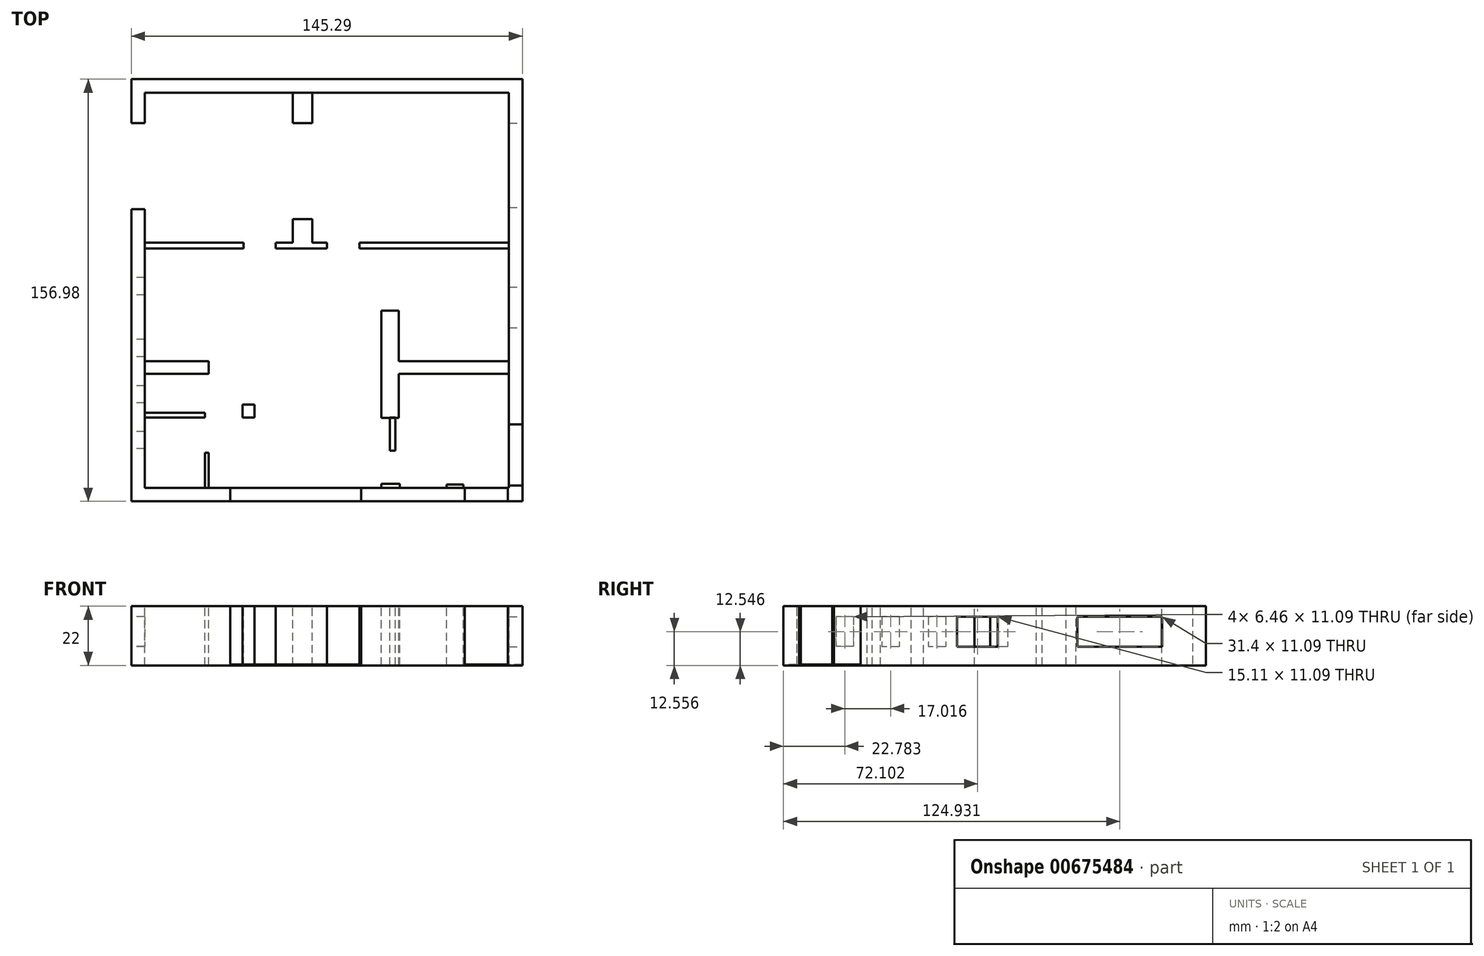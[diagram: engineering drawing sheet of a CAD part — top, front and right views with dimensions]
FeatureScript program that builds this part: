
annotation { "Feature Type Name" : "Feature", "Feature Type Description" : "" }
export const myFeature = defineFeature(function(context is Context, id is Id, definition is map)
    precondition{}
    {
        {
            var Q0;
            Q0=qCreatedBy(makeId("Top.planeOp"),FACE);
            var sketch = newSketch(context, id + "F0", { "sketchPlane" : qUnion([Q0])});
            skLineSegment(sketch, "E0.bottom", {"start": v(-72.65, -85.85) * mm, "end": v(72.64, -85.85) * mm});
            skLineSegment(sketch, "E0.top", {"start": v(-72.65, 71.13) * mm, "end": v(72.64, 71.13) * mm});
            skLineSegment(sketch, "E0.left", {"start": v(-72.65, -85.85) * mm, "end": v(-72.65, 71.13) * mm});
            skLineSegment(sketch, "E0.right", {"start": v(72.64, -85.85) * mm, "end": v(72.64, 71.13) * mm});
            skLineSegment(sketch, "E1.0", {"start": v(-67.65, 66.13) * mm, "end": v(67.64, 66.13) * mm});
            skLineSegment(sketch, "E1.1", {"start": v(-67.65, -80.85) * mm, "end": v(-67.65, 66.13) * mm});
            skLineSegment(sketch, "E1.2", {"start": v(-67.65, -80.85) * mm, "end": v(67.64, -80.85) * mm});
            skLineSegment(sketch, "E1.3", {"start": v(67.64, -80.85) * mm, "end": v(67.64, 66.13) * mm});
            skSolve(sketch);
        }
        {
            var Q0;
            Q0=makeQuery(id+"F0.imprint","IMPRINT",FACE,{"disambiguationData":[TD([[makeQuery(id+"F0.imprint","IMPRINT",EDGE,{"derivedFrom":sQuery(id+"F0.wireOp",EDGE,"E0.bottom")}),1.0]])]});
            extrude(context, id + "F1", {"entities" : qUnion([Q0]), "depth" : 22 * mm, "offsetDistance" : 25 * mm});
        }
        {
            var Q0;
            Q0=makeQuery(id+"F1.opExtrude","CAP_FACE",FACE,{"disambiguationData":[OSD([sQuery(id+"F0.wireOp",EDGE,"E0.bottom"),sQuery(id+"F0.wireOp",EDGE,"E0.top"),sQuery(id+"F0.wireOp",EDGE,"E0.left"),sQuery(id+"F0.wireOp",EDGE,"E0.right"),sQuery(id+"F0.wireOp",EDGE,"E1.0"),sQuery(id+"F0.wireOp",EDGE,"E1.1"),sQuery(id+"F0.wireOp",EDGE,"E1.2"),sQuery(id+"F0.wireOp",EDGE,"E1.3")])],"isStart":false});
            var sketch = newSketch(context, id + "F2", { "sketchPlane" : qUnion([Q0])});
            skLineSegment(sketch, "E2.bottom", {"start": v(-67.65, -33.8) * mm, "end": v(67.64, -33.8) * mm});
            skLineSegment(sketch, "E2.top", {"start": v(-67.65, -38.4) * mm, "end": v(67.64, -38.4) * mm});
            skLineSegment(sketch, "E2.left", {"start": v(-67.65, -33.8) * mm, "end": v(-67.65, -38.4) * mm});
            skLineSegment(sketch, "E2.right", {"start": v(67.64, -33.8) * mm, "end": v(67.64, -38.4) * mm});
            skLineSegment(sketch, "E3.bottom", {"start": v(20.19, -54.82) * mm, "end": v(26.7, -54.82) * mm});
            skLineSegment(sketch, "E3.top", {"start": v(20.19, -14.94) * mm, "end": v(26.7, -14.94) * mm});
            skLineSegment(sketch, "E3.left", {"start": v(20.19, -54.82) * mm, "end": v(20.19, -14.94) * mm});
            skLineSegment(sketch, "E3.right", {"start": v(26.7, -54.82) * mm, "end": v(26.7, -14.94) * mm});
            skLineSegment(sketch, "E4.bottom", {"start": v(-12.7, 66.13) * mm, "end": v(-5.43, 66.13) * mm});
            skLineSegment(sketch, "E4.top", {"start": v(-12.7, 54.76) * mm, "end": v(-5.43, 54.76) * mm});
            skLineSegment(sketch, "E4.left", {"start": v(-12.7, 66.13) * mm, "end": v(-12.7, 54.76) * mm});
            skLineSegment(sketch, "E4.right", {"start": v(-5.43, 66.13) * mm, "end": v(-5.43, 54.76) * mm});
            skLineSegment(sketch, "E5.bottom", {"start": v(-12.7, 19.1) * mm, "end": v(-5.43, 19.1) * mm});
            skLineSegment(sketch, "E5.top", {"start": v(-12.7, 8.13) * mm, "end": v(-5.43, 8.13) * mm});
            skLineSegment(sketch, "E5.left", {"start": v(-12.7, 19.1) * mm, "end": v(-12.7, 8.13) * mm});
            skLineSegment(sketch, "E5.right", {"start": v(-5.43, 19.1) * mm, "end": v(-5.43, 8.13) * mm});
            skLineSegment(sketch, "E6", {"start": v(-43.96, -38.4) * mm, "end": v(-43.96, -33.8) * mm});
            skLineSegment(sketch, "E7.bottom", {"start": v(-67.65, 10.3) * mm, "end": v(67.64, 10.3) * mm});
            skLineSegment(sketch, "E7.top", {"start": v(-67.65, 8.13) * mm, "end": v(67.64, 8.13) * mm});
            skLineSegment(sketch, "E7.left", {"start": v(-67.65, 10.3) * mm, "end": v(-67.65, 8.13) * mm});
            skLineSegment(sketch, "E7.right", {"start": v(67.64, 10.3) * mm, "end": v(67.64, 8.13) * mm});
            skLineSegment(sketch, "E8.bottom", {"start": v(19.78, 8.13) * mm, "end": v(26.7, 8.13) * mm});
            skLineSegment(sketch, "E8.top", {"start": v(19.78, -2.58) * mm, "end": v(26.7, -2.58) * mm});
            skLineSegment(sketch, "E8.left", {"start": v(19.78, 8.13) * mm, "end": v(19.78, -2.58) * mm});
            skLineSegment(sketch, "E8.right", {"start": v(26.7, 8.13) * mm, "end": v(26.7, -2.58) * mm});
            skLineSegment(sketch, "E9.bottom", {"start": v(-43.96, -38.4) * mm, "end": v(-45.35, -38.4) * mm});
            skLineSegment(sketch, "E9.top", {"start": v(-43.96, -80.85) * mm, "end": v(-45.35, -80.85) * mm});
            skLineSegment(sketch, "E9.left", {"start": v(-43.96, -38.4) * mm, "end": v(-43.96, -80.85) * mm});
            skLineSegment(sketch, "E9.right", {"start": v(-45.35, -38.4) * mm, "end": v(-45.35, -80.85) * mm});
            skLineSegment(sketch, "E10.bottom", {"start": v(-67.65, -52.88) * mm, "end": v(-45.35, -52.88) * mm});
            skLineSegment(sketch, "E10.top", {"start": v(-67.65, -54.74) * mm, "end": v(-45.35, -54.74) * mm});
            skLineSegment(sketch, "E10.left", {"start": v(-67.65, -52.88) * mm, "end": v(-67.65, -54.74) * mm});
            skLineSegment(sketch, "E10.right", {"start": v(-45.35, -52.88) * mm, "end": v(-45.35, -54.74) * mm});
            skLineSegment(sketch, "E11.bottom", {"start": v(-45.35, -52.88) * mm, "end": v(-48.5, -52.88) * mm});
            skLineSegment(sketch, "E11.top", {"start": v(-45.35, -49.82) * mm, "end": v(-48.5, -49.82) * mm});
            skLineSegment(sketch, "E11.left", {"start": v(-45.35, -52.88) * mm, "end": v(-45.35, -49.82) * mm});
            skLineSegment(sketch, "E11.right", {"start": v(-48.5, -52.88) * mm, "end": v(-48.5, -49.82) * mm});
            skLineSegment(sketch, "E12.bottom", {"start": v(-31.4, -49.82) * mm, "end": v(-26.87, -49.82) * mm});
            skLineSegment(sketch, "E12.top", {"start": v(-31.4, -54.74) * mm, "end": v(-26.87, -54.74) * mm});
            skLineSegment(sketch, "E12.left", {"start": v(-31.4, -49.82) * mm, "end": v(-31.4, -54.74) * mm});
            skLineSegment(sketch, "E12.right", {"start": v(-26.87, -49.82) * mm, "end": v(-26.87, -54.74) * mm});
            skLineSegment(sketch, "E13.bottom", {"start": v(3.94, -49.82) * mm, "end": v(8.38, -49.82) * mm});
            skLineSegment(sketch, "E13.top", {"start": v(3.94, -54.74) * mm, "end": v(8.38, -54.74) * mm});
            skLineSegment(sketch, "E13.left", {"start": v(3.94, -49.82) * mm, "end": v(3.94, -54.74) * mm});
            skLineSegment(sketch, "E13.right", {"start": v(8.38, -49.82) * mm, "end": v(8.38, -54.74) * mm});
            skPoint(sketch, "E14.firstSnap0", {"position": v(23.45, -54.82) * mm});
            skLineSegment(sketch, "E14.bottom", {"start": v(23.45, -54.74) * mm, "end": v(25.37, -54.74) * mm});
            skLineSegment(sketch, "E14.top", {"start": v(23.45, -67.02) * mm, "end": v(25.37, -67.02) * mm});
            skLineSegment(sketch, "E14.left", {"start": v(23.45, -54.74) * mm, "end": v(23.45, -67.02) * mm});
            skLineSegment(sketch, "E14.right", {"start": v(25.37, -54.74) * mm, "end": v(25.37, -67.02) * mm});
            skLineSegment(sketch, "E15.bottom", {"start": v(47.7, -38.4) * mm, "end": v(49.52, -38.4) * mm});
            skLineSegment(sketch, "E15.top", {"start": v(47.7, -65.4) * mm, "end": v(49.52, -65.4) * mm});
            skLineSegment(sketch, "E15.left", {"start": v(47.7, -38.4) * mm, "end": v(47.7, -65.4) * mm});
            skLineSegment(sketch, "E15.right", {"start": v(49.52, -38.4) * mm, "end": v(49.52, -65.4) * mm});
            skLineSegment(sketch, "E16.bottom", {"start": v(-46.06, -33.8) * mm, "end": v(-43.96, -33.8) * mm});
            skLineSegment(sketch, "E16.top", {"start": v(-46.06, -17.64) * mm, "end": v(-43.96, -17.64) * mm});
            skLineSegment(sketch, "E16.left", {"start": v(-46.06, -33.8) * mm, "end": v(-46.06, -17.64) * mm});
            skLineSegment(sketch, "E16.right", {"start": v(-43.96, -33.8) * mm, "end": v(-43.96, -17.64) * mm});
            skLineSegment(sketch, "E17.bottom", {"start": v(-30.98, 10.3) * mm, "end": v(-19.04, 10.3) * mm});
            skLineSegment(sketch, "E17.top", {"start": v(-30.98, 8.13) * mm, "end": v(-19.04, 8.13) * mm});
            skLineSegment(sketch, "E17.left", {"start": v(-30.98, 10.3) * mm, "end": v(-30.98, 8.13) * mm});
            skLineSegment(sketch, "E17.right", {"start": v(-19.04, 10.3) * mm, "end": v(-19.04, 8.13) * mm});
            skLineSegment(sketch, "E18.bottom", {"start": v(0, 10.3) * mm, "end": v(12.04, 10.3) * mm});
            skLineSegment(sketch, "E18.top", {"start": v(0, 8.13) * mm, "end": v(12.04, 8.13) * mm});
            skLineSegment(sketch, "E18.left", {"start": v(0, 10.3) * mm, "end": v(0, 8.13) * mm});
            skLineSegment(sketch, "E18.right", {"start": v(12.04, 10.3) * mm, "end": v(12.04, 8.13) * mm});
            skLineSegment(sketch, "E19.bottom", {"start": v(-45.35, -39.31) * mm, "end": v(-43.96, -39.31) * mm});
            skLineSegment(sketch, "E19.top", {"start": v(-45.35, -48.84) * mm, "end": v(-43.96, -48.84) * mm});
            skLineSegment(sketch, "E19.left", {"start": v(-45.35, -39.31) * mm, "end": v(-45.35, -48.84) * mm});
            skLineSegment(sketch, "E19.right", {"start": v(-43.96, -39.31) * mm, "end": v(-43.96, -48.84) * mm});
            skLineSegment(sketch, "E20.bottom", {"start": v(-45.35, -56.47) * mm, "end": v(-43.56, -56.47) * mm});
            skLineSegment(sketch, "E20.top", {"start": v(-45.35, -67.73) * mm, "end": v(-43.56, -67.73) * mm});
            skLineSegment(sketch, "E20.left", {"start": v(-45.35, -56.47) * mm, "end": v(-45.35, -67.73) * mm});
            skLineSegment(sketch, "E20.right", {"start": v(-43.56, -56.47) * mm, "end": v(-43.56, -67.73) * mm});
            skLineSegment(sketch, "E21.bottom", {"start": v(20.19, -80.85) * mm, "end": v(27.13, -80.85) * mm});
            skLineSegment(sketch, "E21.top", {"start": v(20.19, -79.38) * mm, "end": v(27.13, -79.38) * mm});
            skLineSegment(sketch, "E21.left", {"start": v(20.19, -80.85) * mm, "end": v(20.19, -79.38) * mm});
            skLineSegment(sketch, "E21.right", {"start": v(27.13, -80.85) * mm, "end": v(27.13, -79.38) * mm});
            skLineSegment(sketch, "E22.bottom", {"start": v(44.44, -80.85) * mm, "end": v(50.77, -80.85) * mm});
            skLineSegment(sketch, "E22.top", {"start": v(44.44, -79.58) * mm, "end": v(50.77, -79.58) * mm});
            skLineSegment(sketch, "E22.left", {"start": v(44.44, -80.85) * mm, "end": v(44.44, -79.58) * mm});
            skLineSegment(sketch, "E22.right", {"start": v(50.77, -80.85) * mm, "end": v(50.77, -79.58) * mm});
            skLineSegment(sketch, "E23.bottom", {"start": v(23.66, -79.38) * mm, "end": v(25.37, -79.38) * mm});
            skLineSegment(sketch, "E23.top", {"start": v(23.66, -77.51) * mm, "end": v(25.37, -77.51) * mm});
            skLineSegment(sketch, "E23.left", {"start": v(23.66, -79.38) * mm, "end": v(23.66, -77.51) * mm});
            skLineSegment(sketch, "E23.right", {"start": v(25.37, -79.38) * mm, "end": v(25.37, -77.51) * mm});
            skLineSegment(sketch, "E24.bottom", {"start": v(47.7, -79.58) * mm, "end": v(49.52, -79.58) * mm});
            skLineSegment(sketch, "E24.top", {"start": v(47.7, -77.8) * mm, "end": v(49.52, -77.8) * mm});
            skLineSegment(sketch, "E24.left", {"start": v(47.7, -79.58) * mm, "end": v(47.7, -77.8) * mm});
            skLineSegment(sketch, "E24.right", {"start": v(49.52, -79.58) * mm, "end": v(49.52, -77.8) * mm});
            skSolve(sketch);
        }
        {
            var Q0;
            {var subQ0=sQuery(id+"F2.wireOp",EDGE,"E2.left");Q0=makeQuery(id+"F2.imprint","IMPRINT",FACE,{"disambiguationData":[TD([[makeQuery(id+"F2.imprint","IMPRINT",EDGE,{"derivedFrom":subQ0}),-1.0]])]});}
            var Q1;
            Q1=makeQuery(id+"F2.imprint","IMPRINT",FACE,{"disambiguationData":[TD([[makeQuery(id+"F2.imprint","IMPRINT",EDGE,{"derivedFrom":sQuery(id+"F2.wireOp",EDGE,"E5.bottom")}),-1.0]])]});
            var Q2;
            Q2=makeQuery(id+"F2.imprint","IMPRINT",FACE,{"disambiguationData":[TD([[makeQuery(id+"F2.imprint","IMPRINT",EDGE,{"derivedFrom":sQuery(id+"F2.wireOp",EDGE,"E4.bottom")}),-1.0]])]});
            var Q3;
            {var subQ5=sQuery(id+"F2.wireOp",EDGE,"E3.top");Q3=makeQuery(id+"F2.imprint","IMPRINT",FACE,{"disambiguationData":[TD([[makeQuery(id+"F2.imprint","IMPRINT",EDGE,{"derivedFrom":subQ5}),-1.0]])]});}
            var Q4;
            {var subQ0=sQuery(id+"F2.wireOp",EDGE,"E3.left");var subQ1=sQuery(id+"F2.wireOp",EDGE,"E2.bottom");var subQ2=makeQuery(id+"F2.imprint","INTERSECT",VERTEX,{"derivedFrom":[subQ1,subQ0]});Q4=makeQuery(id+"F2.imprint","IMPRINT",FACE,{"disambiguationData":[TD([[makeQuery(id+"F2.imprint","IMPRINT",EDGE,{"disambiguationData":[TD([[subQ2,-1.0]])],"derivedFrom":subQ1}),-1.0]])]});}
            var Q5;
            {var subQ5=sQuery(id+"F2.wireOp",EDGE,"E3.bottom");Q5=makeQuery(id+"F2.imprint","IMPRINT",FACE,{"disambiguationData":[TD([[makeQuery(id+"F2.imprint","IMPRINT",EDGE,{"derivedFrom":subQ5}),1.0]])]});}
            var Q6;
            {var subQ0=sQuery(id+"F2.wireOp",EDGE,"E2.right");Q6=makeQuery(id+"F2.imprint","IMPRINT",FACE,{"disambiguationData":[TD([[makeQuery(id+"F2.imprint","IMPRINT",EDGE,{"derivedFrom":subQ0}),1.0]])]});}
            var Q7;
            Q7=makeQuery(id+"F2.imprint","IMPRINT",FACE,{"disambiguationData":[TD([[makeQuery(id+"F2.imprint","IMPRINT",EDGE,{"derivedFrom":sQuery(id+"F2.wireOp",EDGE,"E11.bottom")}),-1.0]])]});
            var Q8;
            {var subQ3=sQuery(id+"F2.wireOp",EDGE,"E10.right");Q8=makeQuery(id+"F2.imprint","IMPRINT",FACE,{"disambiguationData":[TD([[makeQuery(id+"F2.imprint","IMPRINT",EDGE,{"derivedFrom":subQ3}),1.0]])]});}
            var Q9;
            Q9=makeQuery(id+"F2.imprint","IMPRINT",FACE,{"disambiguationData":[TD([[makeQuery(id+"F2.imprint","IMPRINT",EDGE,{"derivedFrom":sQuery(id+"F2.wireOp",EDGE,"E10.bottom")}),-1.0]])]});
            var Q10;
            {var subQ0=sQuery(id+"F2.wireOp",EDGE,"E9.top");Q10=makeQuery(id+"F2.imprint","IMPRINT",FACE,{"disambiguationData":[TD([[makeQuery(id+"F2.imprint","IMPRINT",EDGE,{"derivedFrom":subQ0}),1.0]])]});}
            var Q11;
            Q11=makeQuery(id+"F2.imprint","IMPRINT",FACE,{"disambiguationData":[TD([[makeQuery(id+"F2.imprint","IMPRINT",EDGE,{"derivedFrom":sQuery(id+"F2.wireOp",EDGE,"E12.bottom")}),-1.0]])]});
            var Q12;
            {var subQ0=sQuery(id+"F2.wireOp",EDGE,"E7.left");Q12=makeQuery(id+"F2.imprint","IMPRINT",FACE,{"disambiguationData":[TD([[makeQuery(id+"F2.imprint","IMPRINT",EDGE,{"derivedFrom":subQ0}),-1.0]])]});}
            var Q13;
            {var subQ5=sQuery(id+"F2.wireOp",EDGE,"E17.right");Q13=makeQuery(id+"F2.imprint","IMPRINT",FACE,{"disambiguationData":[TD([[makeQuery(id+"F2.imprint","IMPRINT",EDGE,{"derivedFrom":subQ5}),1.0]])]});}
            var Q14;
            {var subQ0=sQuery(id+"F2.wireOp",EDGE,"E7.top");var subQ1=sQuery(id+"F2.wireOp",EDGE,"E5.left");var subQ2=makeQuery(id+"F2.imprint","INTERSECT",VERTEX,{"derivedFrom":[subQ1,subQ0]});Q14=makeQuery(id+"F2.imprint","IMPRINT",FACE,{"disambiguationData":[TD([[makeQuery(id+"F2.imprint","IMPRINT",EDGE,{"disambiguationData":[TD([[subQ2,1.0]])],"derivedFrom":subQ1}),1.0]])]});}
            var Q15;
            {var subQ5=sQuery(id+"F2.wireOp",EDGE,"E18.left");Q15=makeQuery(id+"F2.imprint","IMPRINT",FACE,{"disambiguationData":[TD([[makeQuery(id+"F2.imprint","IMPRINT",EDGE,{"derivedFrom":subQ5}),-1.0]])]});}
            var Q16;
            {var subQ0=sQuery(id+"F2.wireOp",EDGE,"E7.right");Q16=makeQuery(id+"F2.imprint","IMPRINT",FACE,{"disambiguationData":[TD([[makeQuery(id+"F2.imprint","IMPRINT",EDGE,{"derivedFrom":subQ0}),1.0]])]});}
            var Q17;
            Q17=makeQuery(id+"F2.imprint","IMPRINT",FACE,{"disambiguationData":[TD([[makeQuery(id+"F2.imprint","IMPRINT",EDGE,{"derivedFrom":sQuery(id+"F2.wireOp",EDGE,"E8.bottom")}),-1.0]])]});
            var Q18;
            Q18=makeQuery(id+"F2.imprint","IMPRINT",FACE,{"disambiguationData":[TD([[makeQuery(id+"F2.imprint","IMPRINT",EDGE,{"derivedFrom":sQuery(id+"F2.wireOp",EDGE,"E21.bottom")}),1.0]])]});
            var Q19;
            Q19=makeQuery(id+"F2.imprint","IMPRINT",FACE,{"disambiguationData":[TD([[makeQuery(id+"F2.imprint","IMPRINT",EDGE,{"derivedFrom":sQuery(id+"F2.wireOp",EDGE,"E23.bottom")}),1.0]])]});
            var Q20;
            {var subQ5=sQuery(id+"F2.wireOp",EDGE,"E14.top");Q20=makeQuery(id+"F2.imprint","IMPRINT",FACE,{"disambiguationData":[TD([[makeQuery(id+"F2.imprint","IMPRINT",EDGE,{"derivedFrom":subQ5}),1.0]])]});}
            var Q21;
            Q21=makeQuery(id+"F2.imprint","IMPRINT",FACE,{"disambiguationData":[TD([[makeQuery(id+"F2.imprint","IMPRINT",EDGE,{"derivedFrom":sQuery(id+"F2.wireOp",EDGE,"E15.bottom")}),-1.0]])]});
            var Q22;
            Q22=makeQuery(id+"F2.imprint","IMPRINT",FACE,{"disambiguationData":[TD([[makeQuery(id+"F2.imprint","IMPRINT",EDGE,{"derivedFrom":sQuery(id+"F2.wireOp",EDGE,"E24.bottom")}),1.0]])]});
            var Q23;
            Q23=makeQuery(id+"F2.imprint","IMPRINT",FACE,{"disambiguationData":[TD([[makeQuery(id+"F2.imprint","IMPRINT",EDGE,{"derivedFrom":sQuery(id+"F2.wireOp",EDGE,"E22.bottom")}),1.0]])]});
            extrude(context, id + "F3", {"entities" : qUnion([Q0, Q1, Q2, Q3, Q4, Q5, Q6, Q7, Q8, Q9, Q10, Q11, Q12, Q13, Q14, Q15, Q16, Q17, Q18, Q19, Q20, Q21, Q22, Q23]), "depth" : -22 * mm, "offsetDistance" : 25 * mm});
        }
        {
            var Q0;
            {var subQ0=sQuery(id+"F2.wireOp",EDGE,"E2.left");Q0=makeQuery(id+"F2.imprint","IMPRINT",FACE,{"disambiguationData":[TD([[makeQuery(id+"F2.imprint","IMPRINT",EDGE,{"derivedFrom":subQ0}),1.0]])]});}
            var sketch = newSketch(context, id + "F4", { "sketchPlane" : qUnion([Q0])});
            skLineSegment(sketch, "E25.bottom", {"start": v(-72.61, 54.7) * mm, "end": v(-67.66, 54.7) * mm, "construction": true});
            skLineSegment(sketch, "E25.top", {"start": v(-72.61, 22.74) * mm, "end": v(-67.66, 22.74) * mm, "construction": true});
            skLineSegment(sketch, "E25.left", {"start": v(-72.61, 54.7) * mm, "end": v(-72.61, 22.74) * mm, "construction": true});
            skLineSegment(sketch, "E25.right", {"start": v(-67.66, 54.7) * mm, "end": v(-67.66, 22.74) * mm, "construction": true});
            skLineSegment(sketch, "E26.bottom", {"start": v(-72.78, -1.68) * mm, "end": v(-67.66, -1.68) * mm, "construction": true});
            skLineSegment(sketch, "E26.top", {"start": v(-72.78, -9.03) * mm, "end": v(-67.66, -9.03) * mm, "construction": true});
            skLineSegment(sketch, "E26.left", {"start": v(-72.78, -1.68) * mm, "end": v(-72.78, -9.03) * mm, "construction": true});
            skLineSegment(sketch, "E26.right", {"start": v(-67.66, -1.68) * mm, "end": v(-67.66, -9.03) * mm, "construction": true});
            skLineSegment(sketch, "E27.bottom", {"start": v(-72.7, -25.2) * mm, "end": v(-67.66, -25.2) * mm, "construction": true});
            skLineSegment(sketch, "E27.top", {"start": v(-72.7, -32.75) * mm, "end": v(-67.66, -32.75) * mm, "construction": true});
            skLineSegment(sketch, "E27.left", {"start": v(-72.7, -25.2) * mm, "end": v(-72.7, -32.75) * mm, "construction": true});
            skLineSegment(sketch, "E27.right", {"start": v(-67.66, -25.2) * mm, "end": v(-67.66, -32.75) * mm, "construction": true});
            skLineSegment(sketch, "E28.bottom", {"start": v(67.55, 54.72) * mm, "end": v(72.57, 54.72) * mm, "construction": true});
            skLineSegment(sketch, "E28.top", {"start": v(67.55, 23.12) * mm, "end": v(72.57, 23.12) * mm, "construction": true});
            skLineSegment(sketch, "E28.left", {"start": v(67.55, 54.72) * mm, "end": v(67.55, 23.12) * mm, "construction": true});
            skLineSegment(sketch, "E28.right", {"start": v(72.57, 54.72) * mm, "end": v(72.57, 23.12) * mm, "construction": true});
            skLineSegment(sketch, "E29.bottom", {"start": v(67.66, -6.2) * mm, "end": v(72.57, -6.2) * mm, "construction": true});
            skLineSegment(sketch, "E29.top", {"start": v(67.66, -21.49) * mm, "end": v(72.57, -21.49) * mm, "construction": true});
            skLineSegment(sketch, "E29.left", {"start": v(67.66, -6.2) * mm, "end": v(67.66, -21.49) * mm, "construction": true});
            skLineSegment(sketch, "E29.right", {"start": v(72.57, -6.2) * mm, "end": v(72.57, -21.49) * mm, "construction": true});
            skSolve(sketch);
        }
        {
            var Q0;
            Q0=makeQuery(id+"F1.opExtrude","SWEPT_FACE",FACE,{"disambiguationData":[OSD([sQuery(id+"F0.wireOp",EDGE,"E0.left")])]});
            var sketch = newSketch(context, id + "F5", { "sketchPlane" : qUnion([Q0])});
            skLineSegment(sketch, "E30", {"start": v(-71.13, 0) * mm, "end": v(-71.13, 22) * mm, "construction": true});
            skLineSegment(sketch, "E31", {"start": v(-71.13, 22) * mm, "end": v(-71.13, 7) * mm, "construction": true});
            skLineSegment(sketch, "E32", {"start": v(-71.13, 7) * mm, "end": v(85.85, 7) * mm, "construction": true});
            skLineSegment(sketch, "E33.bottom", {"start": v(-22.72, 22) * mm, "end": v(-54.77, 22) * mm});
            skLineSegment(sketch, "E33.top", {"start": v(-22.72, 0) * mm, "end": v(-54.77, 0) * mm});
            skLineSegment(sketch, "E33.left", {"start": v(-22.72, 22) * mm, "end": v(-22.72, 0) * mm});
            skLineSegment(sketch, "E33.right", {"start": v(-54.77, 22) * mm, "end": v(-54.77, 0) * mm});
            skLineSegment(sketch, "E34", {"start": v(2.6, 22) * mm, "end": v(2.6, 7) * mm, "construction": true});
            skLineSegment(sketch, "E35", {"start": v(2.6, 7) * mm, "end": v(9.06, 22) * mm, "construction": true});
            skLineSegment(sketch, "E36", {"start": v(9.06, 22) * mm, "end": v(9.06, 7) * mm, "construction": true});
            skLineSegment(sketch, "E37", {"start": v(9.06, 7) * mm, "end": v(2.6, 22) * mm, "construction": true});
            skLineSegment(sketch, "E38.bottom", {"start": v(2.6, 7) * mm, "end": v(9.06, 7) * mm, "construction": true});
            skLineSegment(sketch, "E38.top", {"start": v(2.6, 18.1) * mm, "end": v(9.06, 18.1) * mm, "construction": true});
            skLineSegment(sketch, "E38.left", {"start": v(2.6, 7) * mm, "end": v(2.6, 18.1) * mm, "construction": true});
            skLineSegment(sketch, "E38.right", {"start": v(9.06, 7) * mm, "end": v(9.06, 18.1) * mm, "construction": true});
            skLineSegment(sketch, "E39.bottom", {"start": v(2.6, 18.1) * mm, "end": v(9.06, 18.1) * mm});
            skLineSegment(sketch, "E39.top", {"start": v(2.6, 7) * mm, "end": v(9.06, 7) * mm});
            skLineSegment(sketch, "E39.left", {"start": v(2.6, 18.1) * mm, "end": v(2.6, 7) * mm});
            skLineSegment(sketch, "E39.right", {"start": v(9.06, 18.1) * mm, "end": v(9.06, 7) * mm});
            skLineSegment(sketch, "E40.bottom", {"start": v(25.6, 7) * mm, "end": v(32.06, 7) * mm, "construction": true});
            skLineSegment(sketch, "E40.top", {"start": v(25.6, 18.1) * mm, "end": v(32.06, 18.1) * mm, "construction": true});
            skLineSegment(sketch, "E40.left", {"start": v(25.6, 7) * mm, "end": v(25.6, 18.1) * mm, "construction": true});
            skLineSegment(sketch, "E40.right", {"start": v(32.06, 7) * mm, "end": v(32.06, 18.1) * mm, "construction": true});
            skLineSegment(sketch, "E41.bottom", {"start": v(25.6, 18.1) * mm, "end": v(32.06, 18.1) * mm});
            skLineSegment(sketch, "E41.top", {"start": v(25.6, 7) * mm, "end": v(32.06, 7) * mm});
            skLineSegment(sketch, "E41.left", {"start": v(25.6, 18.1) * mm, "end": v(25.6, 7) * mm});
            skLineSegment(sketch, "E41.right", {"start": v(32.06, 18.1) * mm, "end": v(32.06, 7) * mm});
            skLineSegment(sketch, "E42", {"start": v(42.82, 22) * mm, "end": v(42.82, 7) * mm, "construction": true});
            skLineSegment(sketch, "E43", {"start": v(42.82, 7) * mm, "end": v(49.28, 22) * mm, "construction": true});
            skLineSegment(sketch, "E44", {"start": v(49.28, 22) * mm, "end": v(49.28, 7) * mm, "construction": true});
            skLineSegment(sketch, "E45", {"start": v(49.28, 7) * mm, "end": v(42.82, 22) * mm, "construction": true});
            skLineSegment(sketch, "E46.bottom", {"start": v(42.82, 7) * mm, "end": v(49.28, 7) * mm, "construction": true});
            skLineSegment(sketch, "E46.top", {"start": v(42.82, 18.09) * mm, "end": v(49.28, 18.09) * mm, "construction": true});
            skLineSegment(sketch, "E46.left", {"start": v(42.82, 7) * mm, "end": v(42.82, 18.09) * mm, "construction": true});
            skLineSegment(sketch, "E46.right", {"start": v(49.28, 7) * mm, "end": v(49.28, 18.09) * mm, "construction": true});
            skLineSegment(sketch, "E47.bottom", {"start": v(42.82, 18.09) * mm, "end": v(49.28, 18.09) * mm});
            skLineSegment(sketch, "E47.top", {"start": v(42.82, 7) * mm, "end": v(49.28, 7) * mm});
            skLineSegment(sketch, "E47.left", {"start": v(42.82, 18.09) * mm, "end": v(42.82, 7) * mm});
            skLineSegment(sketch, "E47.right", {"start": v(49.28, 18.09) * mm, "end": v(49.28, 7) * mm});
            skLineSegment(sketch, "E48.bottom", {"start": v(59.84, 7) * mm, "end": v(66.3, 7) * mm, "construction": true});
            skLineSegment(sketch, "E48.top", {"start": v(59.84, 18.1) * mm, "end": v(66.3, 18.1) * mm, "construction": true});
            skLineSegment(sketch, "E48.left", {"start": v(59.84, 7) * mm, "end": v(59.84, 18.1) * mm, "construction": true});
            skLineSegment(sketch, "E48.right", {"start": v(66.3, 7) * mm, "end": v(66.3, 18.1) * mm, "construction": true});
            skLineSegment(sketch, "E49.bottom", {"start": v(59.84, 18.1) * mm, "end": v(66.3, 18.1) * mm});
            skLineSegment(sketch, "E49.top", {"start": v(59.84, 7) * mm, "end": v(66.3, 7) * mm});
            skLineSegment(sketch, "E49.left", {"start": v(59.84, 18.1) * mm, "end": v(59.84, 7) * mm});
            skLineSegment(sketch, "E49.right", {"start": v(66.3, 18.1) * mm, "end": v(66.3, 7) * mm});
            skSolve(sketch);
        }
        {
            var Q0;
            Q0=makeQuery(id+"F5.imprint","IMPRINT",FACE,{"disambiguationData":[TD([[makeQuery(id+"F5.imprint","IMPRINT",EDGE,{"derivedFrom":sQuery(id+"F5.wireOp",EDGE,"E33.bottom")}),1.0]])]});
            var Q1;
            Q1=makeQuery(id+"F5.imprint","IMPRINT",FACE,{"disambiguationData":[TD([[makeQuery(id+"F5.imprint","IMPRINT",EDGE,{"derivedFrom":sQuery(id+"F5.wireOp",EDGE,"E39.bottom")}),-1.0]])]});
            var Q2;
            Q2=makeQuery(id+"F5.imprint","IMPRINT",FACE,{"disambiguationData":[TD([[makeQuery(id+"F5.imprint","IMPRINT",EDGE,{"derivedFrom":sQuery(id+"F5.wireOp",EDGE,"E41.bottom")}),-1.0]])]});
            var Q3;
            Q3=makeQuery(id+"F5.imprint","IMPRINT",FACE,{"disambiguationData":[TD([[makeQuery(id+"F5.imprint","IMPRINT",EDGE,{"derivedFrom":sQuery(id+"F5.wireOp",EDGE,"E47.bottom")}),-1.0]])]});
            var Q4;
            Q4=makeQuery(id+"F5.imprint","IMPRINT",FACE,{"disambiguationData":[TD([[makeQuery(id+"F5.imprint","IMPRINT",EDGE,{"derivedFrom":sQuery(id+"F5.wireOp",EDGE,"E49.bottom")}),-1.0]])]});
            extrude(context, id + "F6", {"entities" : qUnion([Q0, Q1, Q2, Q3, Q4]), "operationType" : NewBodyOperationType.REMOVE, "oppositeDirection" : true, "depth" : 8.3 * mm, "offsetDistance" : 25 * mm});
        }
        {
            var Q0;
            Q0=makeQuery(id+"F1.opExtrude","SWEPT_FACE",FACE,{"disambiguationData":[OSD([sQuery(id+"F0.wireOp",EDGE,"E0.right")])]});
            var sketch = newSketch(context, id + "F7", { "sketchPlane" : qUnion([Q0])});
            skLineSegment(sketch, "E50", {"start": v(71.13, 22) * mm, "end": v(71.13, 7) * mm, "construction": true});
            skLineSegment(sketch, "E51.bottom", {"start": v(35.6, 7) * mm, "end": v(54.72, 7) * mm, "construction": true});
            skLineSegment(sketch, "E51.top", {"start": v(23.38, 18.1) * mm, "end": v(54.72, 18.1) * mm, "construction": true});
            skLineSegment(sketch, "E51.right", {"start": v(54.72, 7) * mm, "end": v(54.72, 18.1) * mm, "construction": true});
            skLineSegment(sketch, "E52.bottom", {"start": v(23.38, 18.1) * mm, "end": v(54.78, 18.1) * mm});
            skLineSegment(sketch, "E52.top", {"start": v(23.38, 7) * mm, "end": v(54.78, 7) * mm});
            skLineSegment(sketch, "E52.left", {"start": v(23.38, 18.1) * mm, "end": v(23.38, 7) * mm});
            skLineSegment(sketch, "E52.right", {"start": v(54.78, 18.1) * mm, "end": v(54.78, 7) * mm});
            skLineSegment(sketch, "E53", {"start": v(71.13, 7) * mm, "end": v(-80.41, 7) * mm, "construction": true});
            skLineSegment(sketch, "E54", {"start": v(30.08, 18.1) * mm, "end": v(-62.34, 18.1) * mm, "construction": true});
            skLineSegment(sketch, "E55.bottom", {"start": v(-21.3, 18.1) * mm, "end": v(-6.2, 18.1) * mm});
            skLineSegment(sketch, "E55.top", {"start": v(-21.3, 7) * mm, "end": v(-6.2, 7) * mm});
            skLineSegment(sketch, "E55.left", {"start": v(-21.3, 18.1) * mm, "end": v(-21.3, 7) * mm});
            skLineSegment(sketch, "E55.right", {"start": v(-6.2, 18.1) * mm, "end": v(-6.2, 7) * mm});
            skSolve(sketch);
        }
        {
            var Q0;
            Q0=makeQuery(id+"F7.imprint","IMPRINT",FACE,{"disambiguationData":[TD([[makeQuery(id+"F7.imprint","IMPRINT",EDGE,{"derivedFrom":sQuery(id+"F7.wireOp",EDGE,"E55.bottom")}),-1.0]])]});
            var Q1;
            Q1=makeQuery(id+"F7.imprint","IMPRINT",FACE,{"disambiguationData":[TD([[makeQuery(id+"F7.imprint","IMPRINT",EDGE,{"derivedFrom":sQuery(id+"F7.wireOp",EDGE,"E52.bottom")}),-1.0]])]});
            extrude(context, id + "F8", {"entities" : qUnion([Q0, Q1]), "operationType" : NewBodyOperationType.REMOVE, "oppositeDirection" : true, "depth" : 9.5 * mm, "offsetDistance" : 25 * mm});
        }
        {
            var Q0;
            {var subQ8=sQuery(id+"F2.wireOp",EDGE,"E2.left");Q0=makeQuery(id+"F4.imprint","IMPRINT",FACE,{"disambiguationData":[TD([[makeQuery(id+"F4.imprint","IMPRINT",EDGE,{"derivedFrom":makeQuery(id+"F2.imprint","IMPRINT",EDGE,{"derivedFrom":subQ8})}),1.0]])]});}
            var sketch = newSketch(context, id + "F9", { "sketchPlane" : qUnion([Q0])});
            skLineSegment(sketch, "E56.bottom", {"start": v(-35.86, -80.58) * mm, "end": v(12.74, -80.58) * mm});
            skLineSegment(sketch, "E56.top", {"start": v(-35.86, -86.5) * mm, "end": v(12.74, -86.5) * mm});
            skLineSegment(sketch, "E56.left", {"start": v(-35.86, -80.58) * mm, "end": v(-35.86, -86.5) * mm});
            skLineSegment(sketch, "E56.right", {"start": v(12.74, -80.58) * mm, "end": v(12.74, -86.5) * mm});
            skLineSegment(sketch, "E57.bottom", {"start": v(51.19, -79.9) * mm, "end": v(67.27, -79.9) * mm});
            skLineSegment(sketch, "E57.top", {"start": v(51.19, -87.42) * mm, "end": v(67.27, -87.42) * mm});
            skLineSegment(sketch, "E57.left", {"start": v(51.19, -79.9) * mm, "end": v(51.19, -87.42) * mm});
            skLineSegment(sketch, "E57.right", {"start": v(67.27, -79.9) * mm, "end": v(67.27, -87.42) * mm});
            skLineSegment(sketch, "E58.bottom", {"start": v(75.49, -80) * mm, "end": v(61.34, -80) * mm});
            skLineSegment(sketch, "E58.top", {"start": v(75.49, -57.19) * mm, "end": v(61.34, -57.19) * mm});
            skLineSegment(sketch, "E58.left", {"start": v(75.49, -80) * mm, "end": v(75.49, -57.19) * mm});
            skLineSegment(sketch, "E58.right", {"start": v(61.34, -80) * mm, "end": v(61.34, -57.19) * mm});
            skSolve(sketch);
        }
        {
            var Q0;
            Q0 = qSketchRegion(id + "F9", true);
            extrude(context, id + "F10", {"entities" : qUnion([Q0]), "operationType" : NewBodyOperationType.REMOVE, "oppositeDirection" : true, "depth" : 21.6 * mm, "offsetDistance" : 25 * mm});
        }
    });
